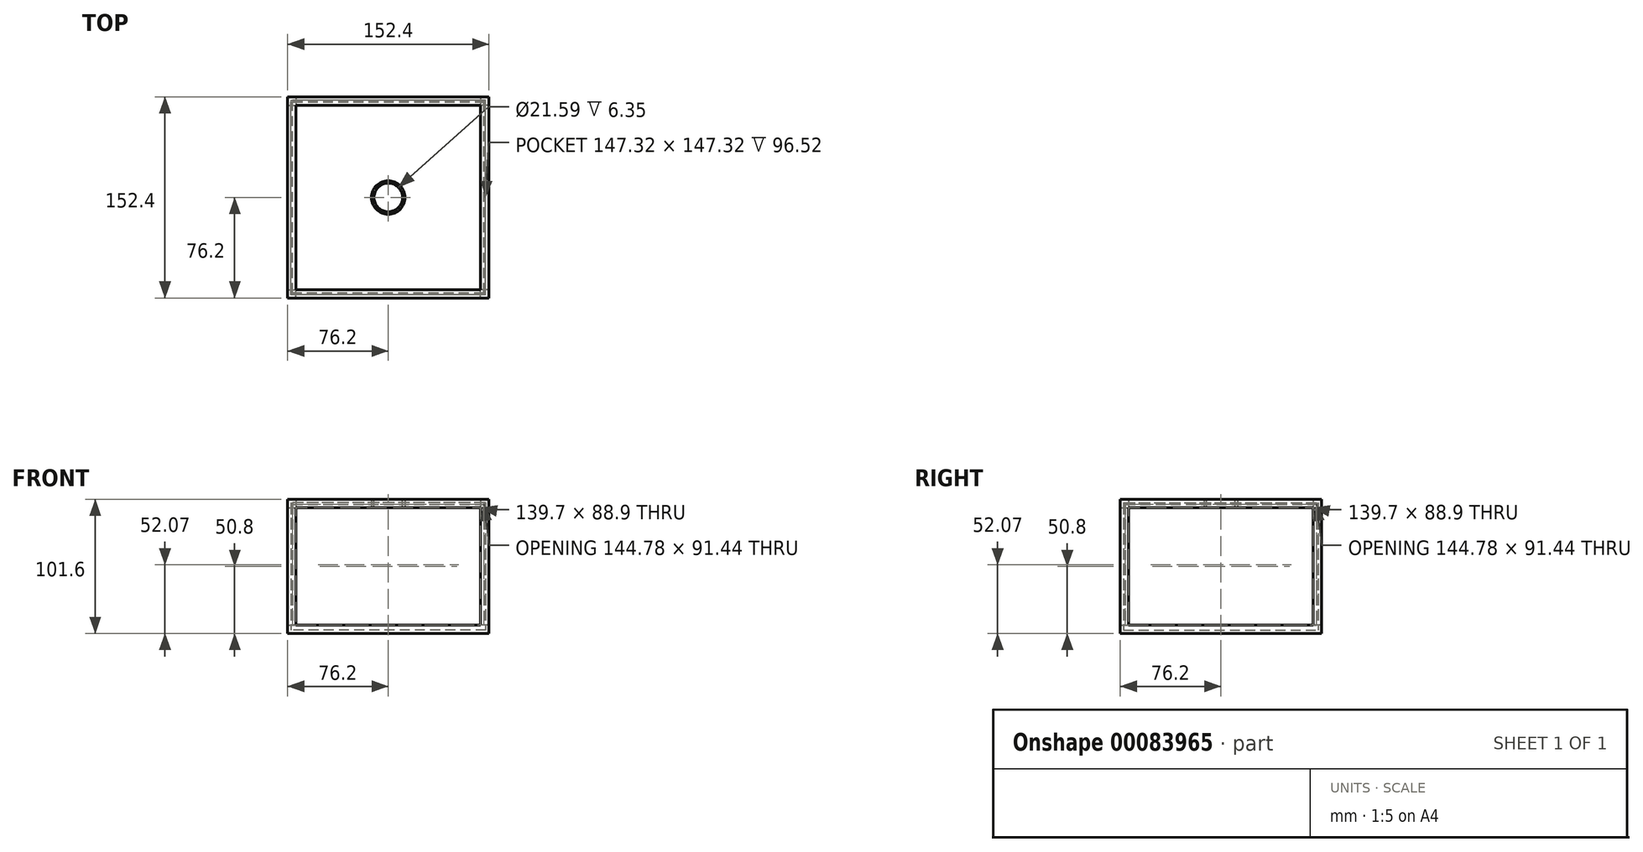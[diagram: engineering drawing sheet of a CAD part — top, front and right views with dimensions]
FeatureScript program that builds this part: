
annotation { "Feature Type Name" : "Feature", "Feature Type Description" : "" }
export const myFeature = defineFeature(function(context is Context, id is Id, definition is map)
    precondition{}
    {
        {
            var Q0;
            Q0=qCreatedBy(makeId("Top.planeOp"),FACE);
            var sketch = newSketch(context, id + "F0", { "sketchPlane" : qUnion([Q0])});
            skLineSegment(sketch, "E0.bottom", {"start": v(76.2, -76.2) * mm, "end": v(-76.2, -76.2) * mm});
            skLineSegment(sketch, "E0.top", {"start": v(76.2, 76.2) * mm, "end": v(-76.2, 76.2) * mm});
            skLineSegment(sketch, "E0.left", {"start": v(76.2, -76.2) * mm, "end": v(76.2, 76.2) * mm});
            skLineSegment(sketch, "E0.right", {"start": v(-76.2, -76.2) * mm, "end": v(-76.2, 76.2) * mm});
            skPoint(sketch, "E0.middle", {"position": v(0, 0) * mm});
            skSolve(sketch);
        }
        {
            var Q0;
            Q0 = qSketchRegion(id + "F0", true);
            extrude(context, id + "F1", {"entities" : qUnion([Q0]), "depth" : 6.35 * mm});
        }
        {
            var Q0;
            Q0=makeQuery(id+"F1.opExtrude","CAP_FACE",FACE,{"disambiguationData":[OSD([sQuery(id+"F0.wireOp",EDGE,"E0.bottom"),sQuery(id+"F0.wireOp",EDGE,"E0.top"),sQuery(id+"F0.wireOp",EDGE,"E0.left"),sQuery(id+"F0.wireOp",EDGE,"E0.right")])],"isStart":false});
            var sketch = newSketch(context, id + "F2", { "sketchPlane" : qUnion([Q0])});
            skLineSegment(sketch, "E1.bottom", {"start": v(76.2, -76.2) * mm, "end": v(69.85, -76.2) * mm});
            skLineSegment(sketch, "E1.top", {"start": v(76.2, -69.85) * mm, "end": v(69.85, -69.85) * mm});
            skLineSegment(sketch, "E1.left", {"start": v(76.2, -76.2) * mm, "end": v(76.2, -69.85) * mm});
            skLineSegment(sketch, "E1.right", {"start": v(69.85, -76.2) * mm, "end": v(69.85, -69.85) * mm});
            skSolve(sketch);
        }
        {
            var Q0;
            Q0 = qSketchRegion(id + "F2", true);
            extrude(context, id + "F3", {"entities" : qUnion([Q0]), "operationType" : NewBodyOperationType.ADD, "depth" : 95.25 * mm});
        }
        {
            var Q0;
            Q0=makeQuery(id+"F1.opExtrude","CAP_FACE",FACE,{"disambiguationData":[OSD([sQuery(id+"F0.wireOp",EDGE,"E0.bottom"),sQuery(id+"F0.wireOp",EDGE,"E0.top"),sQuery(id+"F0.wireOp",EDGE,"E0.left"),sQuery(id+"F0.wireOp",EDGE,"E0.right")])],"isStart":false});
            var sketch = newSketch(context, id + "F4", { "sketchPlane" : qUnion([Q0])});
            skLineSegment(sketch, "E2.bottom", {"start": v(76.2, 76.2) * mm, "end": v(69.85, 76.2) * mm});
            skLineSegment(sketch, "E2.top", {"start": v(76.2, 69.85) * mm, "end": v(69.85, 69.85) * mm});
            skLineSegment(sketch, "E2.left", {"start": v(76.2, 76.2) * mm, "end": v(76.2, 69.85) * mm});
            skLineSegment(sketch, "E2.right", {"start": v(69.85, 76.2) * mm, "end": v(69.85, 69.85) * mm});
            skSolve(sketch);
        }
        {
            var Q0;
            Q0 = qSketchRegion(id + "F4", true);
            extrude(context, id + "F5", {"entities" : qUnion([Q0]), "operationType" : NewBodyOperationType.ADD, "depth" : 95.25 * mm});
        }
        {
            var Q0;
            Q0=makeQuery(id+"F1.opExtrude","CAP_FACE",FACE,{"disambiguationData":[OSD([sQuery(id+"F0.wireOp",EDGE,"E0.bottom"),sQuery(id+"F0.wireOp",EDGE,"E0.top"),sQuery(id+"F0.wireOp",EDGE,"E0.left"),sQuery(id+"F0.wireOp",EDGE,"E0.right")])],"isStart":false});
            var sketch = newSketch(context, id + "F6", { "sketchPlane" : qUnion([Q0])});
            skLineSegment(sketch, "E3.bottom", {"start": v(-76.2, 76.2) * mm, "end": v(-69.85, 76.2) * mm});
            skLineSegment(sketch, "E3.top", {"start": v(-76.2, 69.85) * mm, "end": v(-69.85, 69.85) * mm});
            skLineSegment(sketch, "E3.left", {"start": v(-76.2, 76.2) * mm, "end": v(-76.2, 69.85) * mm});
            skLineSegment(sketch, "E3.right", {"start": v(-69.85, 76.2) * mm, "end": v(-69.85, 69.85) * mm});
            skSolve(sketch);
        }
        {
            var Q0;
            Q0=makeQuery(id+"F6.imprint","IMPRINT",FACE,{"disambiguationData":[TD([[makeQuery(id+"F6.imprint","IMPRINT",EDGE,{"derivedFrom":sQuery(id+"F6.wireOp",EDGE,"E3.bottom")}),1.0]])]});
            extrude(context, id + "F7", {"entities" : qUnion([Q0]), "operationType" : NewBodyOperationType.ADD, "depth" : 95.25 * mm});
        }
        {
            var Q0;
            Q0=makeQuery(id+"F1.opExtrude","CAP_FACE",FACE,{"disambiguationData":[OSD([sQuery(id+"F0.wireOp",EDGE,"E0.bottom"),sQuery(id+"F0.wireOp",EDGE,"E0.top"),sQuery(id+"F0.wireOp",EDGE,"E0.left"),sQuery(id+"F0.wireOp",EDGE,"E0.right")])],"isStart":false});
            var sketch = newSketch(context, id + "F8", { "sketchPlane" : qUnion([Q0])});
            skLineSegment(sketch, "E4.bottom", {"start": v(-76.2, -76.2) * mm, "end": v(-69.85, -76.2) * mm});
            skLineSegment(sketch, "E4.top", {"start": v(-76.2, -69.85) * mm, "end": v(-69.85, -69.85) * mm});
            skLineSegment(sketch, "E4.left", {"start": v(-76.2, -76.2) * mm, "end": v(-76.2, -69.85) * mm});
            skLineSegment(sketch, "E4.right", {"start": v(-69.85, -76.2) * mm, "end": v(-69.85, -69.85) * mm});
            skSolve(sketch);
        }
        {
            var Q0;
            Q0=makeQuery(id+"F8.imprint","IMPRINT",FACE,{"disambiguationData":[TD([[makeQuery(id+"F8.imprint","IMPRINT",EDGE,{"derivedFrom":sQuery(id+"F8.wireOp",EDGE,"E4.bottom")}),-1.0]])]});
            extrude(context, id + "F9", {"entities" : qUnion([Q0]), "operationType" : NewBodyOperationType.ADD, "depth" : 95.25 * mm});
        }
        {
            var Q0;
            Q0=makeQuery(id+"F5.opExtrude","SWEPT_FACE",FACE,{"disambiguationData":[OSD([sQuery(id+"F4.wireOp",EDGE,"E2.right")])]});
            var sketch = newSketch(context, id + "F10", { "sketchPlane" : qUnion([Q0])});
            skLineSegment(sketch, "E5.bottom", {"start": v(-76.2, 101.6) * mm, "end": v(-69.85, 101.6) * mm});
            skLineSegment(sketch, "E5.top", {"start": v(-76.2, 95.25) * mm, "end": v(-69.85, 95.25) * mm});
            skLineSegment(sketch, "E5.left", {"start": v(-76.2, 101.6) * mm, "end": v(-76.2, 95.25) * mm});
            skLineSegment(sketch, "E5.right", {"start": v(-69.85, 101.6) * mm, "end": v(-69.85, 95.25) * mm});
            skSolve(sketch);
        }
        {
            var Q0;
            Q0 = qSketchRegion(id + "F10", true);
            extrude(context, id + "F11", {"entities" : qUnion([Q0]), "operationType" : NewBodyOperationType.ADD, "depth" : 139.7 * mm});
        }
        {
            var Q0;
            Q0=makeQuery(id+"F11.boolean.opBoolean","MERGE",FACE,{"derivedFrom":[makeQuery(id+"F5.opExtrude","SWEPT_FACE",FACE,{"disambiguationData":[OSD([sQuery(id+"F4.wireOp",EDGE,"E2.top")])]}),makeQuery(id+"F7.opExtrude","SWEPT_FACE",FACE,{"disambiguationData":[OSD([sQuery(id+"F6.wireOp",EDGE,"E3.top")])]}),makeQuery(id+"F11.opExtrude","SWEPT_FACE",FACE,{"disambiguationData":[OSD([sQuery(id+"F10.wireOp",EDGE,"E5.right")])]})]});
            var sketch = newSketch(context, id + "F12", { "sketchPlane" : qUnion([Q0])});
            skLineSegment(sketch, "E6.bottom", {"start": v(-76.2, 101.6) * mm, "end": v(-69.85, 101.6) * mm});
            skLineSegment(sketch, "E6.top", {"start": v(-76.2, 95.25) * mm, "end": v(-69.85, 95.25) * mm});
            skLineSegment(sketch, "E6.left", {"start": v(-76.2, 101.6) * mm, "end": v(-76.2, 95.25) * mm});
            skLineSegment(sketch, "E6.right", {"start": v(-69.85, 101.6) * mm, "end": v(-69.85, 95.25) * mm});
            skSolve(sketch);
        }
        {
            var Q0;
            Q0=makeQuery(id+"F12.imprint","IMPRINT",FACE,{"disambiguationData":[TD([[makeQuery(id+"F12.imprint","IMPRINT",EDGE,{"derivedFrom":sQuery(id+"F12.wireOp",EDGE,"E6.bottom")}),1.0]])]});
            extrude(context, id + "F13", {"entities" : qUnion([Q0]), "operationType" : NewBodyOperationType.ADD, "depth" : 139.7 * mm});
        }
        {
            var Q0;
            Q0=makeQuery(id+"F13.boolean.opBoolean","MERGE",FACE,{"derivedFrom":[makeQuery(id+"F9.opExtrude","SWEPT_FACE",FACE,{"disambiguationData":[OSD([sQuery(id+"F8.wireOp",EDGE,"E4.right")])]}),makeQuery(id+"F13.opExtrude","SWEPT_FACE",FACE,{"disambiguationData":[OSD([sQuery(id+"F12.wireOp",EDGE,"E6.right")])]})]});
            var sketch = newSketch(context, id + "F14", { "sketchPlane" : qUnion([Q0])});
            skLineSegment(sketch, "E7.bottom", {"start": v(-76.2, 101.6) * mm, "end": v(-69.85, 101.6) * mm});
            skLineSegment(sketch, "E7.top", {"start": v(-76.2, 95.25) * mm, "end": v(-69.85, 95.25) * mm});
            skLineSegment(sketch, "E7.left", {"start": v(-76.2, 101.6) * mm, "end": v(-76.2, 95.25) * mm});
            skLineSegment(sketch, "E7.right", {"start": v(-69.85, 101.6) * mm, "end": v(-69.85, 95.25) * mm});
            skSolve(sketch);
        }
        {
            var Q0;
            Q0=makeQuery(id+"F14.imprint","IMPRINT",FACE,{"disambiguationData":[TD([[makeQuery(id+"F14.imprint","IMPRINT",EDGE,{"derivedFrom":sQuery(id+"F14.wireOp",EDGE,"E7.bottom")}),-1.0]])]});
            extrude(context, id + "F15", {"entities" : qUnion([Q0]), "operationType" : NewBodyOperationType.ADD, "depth" : 139.7 * mm});
        }
        {
            var Q0;
            {var subQ1=sQuery(id+"F6.wireOp",EDGE,"E3.top");var subQ2=makeQuery(id+"F7.opExtrude","SWEPT_FACE",FACE,{"disambiguationData":[OSD([subQ1])]});var subQ4=sQuery(id+"F4.wireOp",EDGE,"E2.top");var subQ5=makeQuery(id+"F5.opExtrude","SWEPT_FACE",FACE,{"disambiguationData":[OSD([subQ4])]});var subQ7=makeQuery(id+"F11.opExtrude","SWEPT_FACE",FACE,{"disambiguationData":[OSD([sQuery(id+"F10.wireOp",EDGE,"E5.right")])]});var subQ8=sQuery(id+"F0.wireOp",EDGE,"E0.left");Q0=makeQuery(id+"F13.boolean.opBoolean","SPLIT",FACE,{"disambiguationData":[TD([makeQuery(id+"F1.opExtrude","SWEPT_FACE",FACE,{"disambiguationData":[OSD([subQ8])]})])],"derivedFrom":makeQuery(id+"F11.boolean.opBoolean","MERGE",FACE,{"derivedFrom":[subQ5,subQ2,subQ7]})});}
            var sketch = newSketch(context, id + "F16", { "sketchPlane" : qUnion([Q0])});
            skLineSegment(sketch, "E8.bottom", {"start": v(76.2, 101.6) * mm, "end": v(69.85, 101.6) * mm});
            skLineSegment(sketch, "E8.top", {"start": v(76.2, 95.25) * mm, "end": v(69.85, 95.25) * mm});
            skLineSegment(sketch, "E8.left", {"start": v(76.2, 101.6) * mm, "end": v(76.2, 95.25) * mm});
            skLineSegment(sketch, "E8.right", {"start": v(69.85, 101.6) * mm, "end": v(69.85, 95.25) * mm});
            skSolve(sketch);
        }
        {
            var Q0;
            Q0 = qSketchRegion(id + "F16", true);
            extrude(context, id + "F17", {"entities" : qUnion([Q0]), "operationType" : NewBodyOperationType.ADD, "depth" : 139.7 * mm});
        }
        {
            var Q0;
            Q0=makeQuery(id+"F1.opExtrude","CAP_FACE",FACE,{"disambiguationData":[OSD([sQuery(id+"F0.wireOp",EDGE,"E0.bottom"),sQuery(id+"F0.wireOp",EDGE,"E0.top"),sQuery(id+"F0.wireOp",EDGE,"E0.left"),sQuery(id+"F0.wireOp",EDGE,"E0.right")])],"isStart":false});
            shell(context, id + "F18", {"entities" : qUnion([Q0]), "thickness" : 2.54 * mm});
        }
        {
            var Q0;
            {var subQ0=sQuery(id+"F0.wireOp",EDGE,"E0.right");var subQ1=sQuery(id+"F0.wireOp",EDGE,"E0.left");var subQ2=sQuery(id+"F0.wireOp",EDGE,"E0.top");var subQ3=sQuery(id+"F0.wireOp",EDGE,"E0.bottom");Q0=makeQuery(id+"F18.opShell","OFFSET_FACE",FACE,{"disambiguationData":[OSD([subQ3,subQ2,subQ1,subQ0]),TDD([makeQuery(id+"F1.opExtrude","CAP_FACE",FACE,{"disambiguationData":[OSD([subQ3,subQ2,subQ1,subQ0])],"isStart":true})])]});}
            var sketch = newSketch(context, id + "F19", { "sketchPlane" : qUnion([Q0])});
            skCircle(sketch, "E9", {"center": v(0, 0) * mm, "radius": 12.7 * mm});
            skSolve(sketch);
        }
        {
            var Q0;
            Q0=sQuery(id+"F19.wireOp",EDGE,"E9");
            extrude(context, id + "F20", {"bodyType" : ToolBodyType.SURFACE, "surfaceEntities" : qUnion([Q0]), "depth" : 6.35 * mm});
        }
        {
            var Q0;
            Q0=qCreatedBy(makeId("Top.planeOp"),FACE);
            cPlane(context, id + "F21", {"entities" : qUnion([Q0]), "cplaneType" : CPlaneType.OFFSET, "offset" : 95.25 * mm, "width" : 152.4 * mm, "height" : 152.4 * mm});
        }
        {
            var Q0;
            Q0=qCreatedBy(id+"F21.planeOp",FACE);
            var sketch = newSketch(context, id + "F22", { "sketchPlane" : qUnion([Q0])});
            skCircle(sketch, "E10", {"center": v(0, 0) * mm, "radius": 12.7 * mm});
            skSolve(sketch);
        }
        {
            var Q0;
            Q0=makeQuery(id+"F22.imprint","IMPRINT",FACE,{"disambiguationData":[TD([[makeQuery(id+"F22.imprint","IMPRINT",EDGE,{"derivedFrom":sQuery(id+"F22.wireOp",EDGE,"E10")}),1.0]])]});
            extrude(context, id + "F23", {"entities" : qUnion([Q0]), "depth" : 6.35 * mm});
        }
        {
            var Q0;
            Q0=makeQuery(id+"F23.opExtrude","CAP_FACE",FACE,{"disambiguationData":[OSD([sQuery(id+"F22.wireOp",EDGE,"E10")])],"isStart":false});
            var sketch = newSketch(context, id + "F24", { "sketchPlane" : qUnion([Q0])});
            skCircle(sketch, "E11", {"center": v(0, 0) * mm, "radius": 10.8 * mm});
            skSolve(sketch);
        }
        {
            var Q0;
            Q0=makeQuery(id+"F24.imprint","IMPRINT",FACE,{"disambiguationData":[TD([[makeQuery(id+"F24.imprint","IMPRINT",EDGE,{"derivedFrom":sQuery(id+"F24.wireOp",EDGE,"E11")}),1.0]])]});
            extrude(context, id + "F25", {"entities" : qUnion([Q0]), "operationType" : NewBodyOperationType.REMOVE, "oppositeDirection" : true, "depth" : 25.4 * mm});
        }
    });
